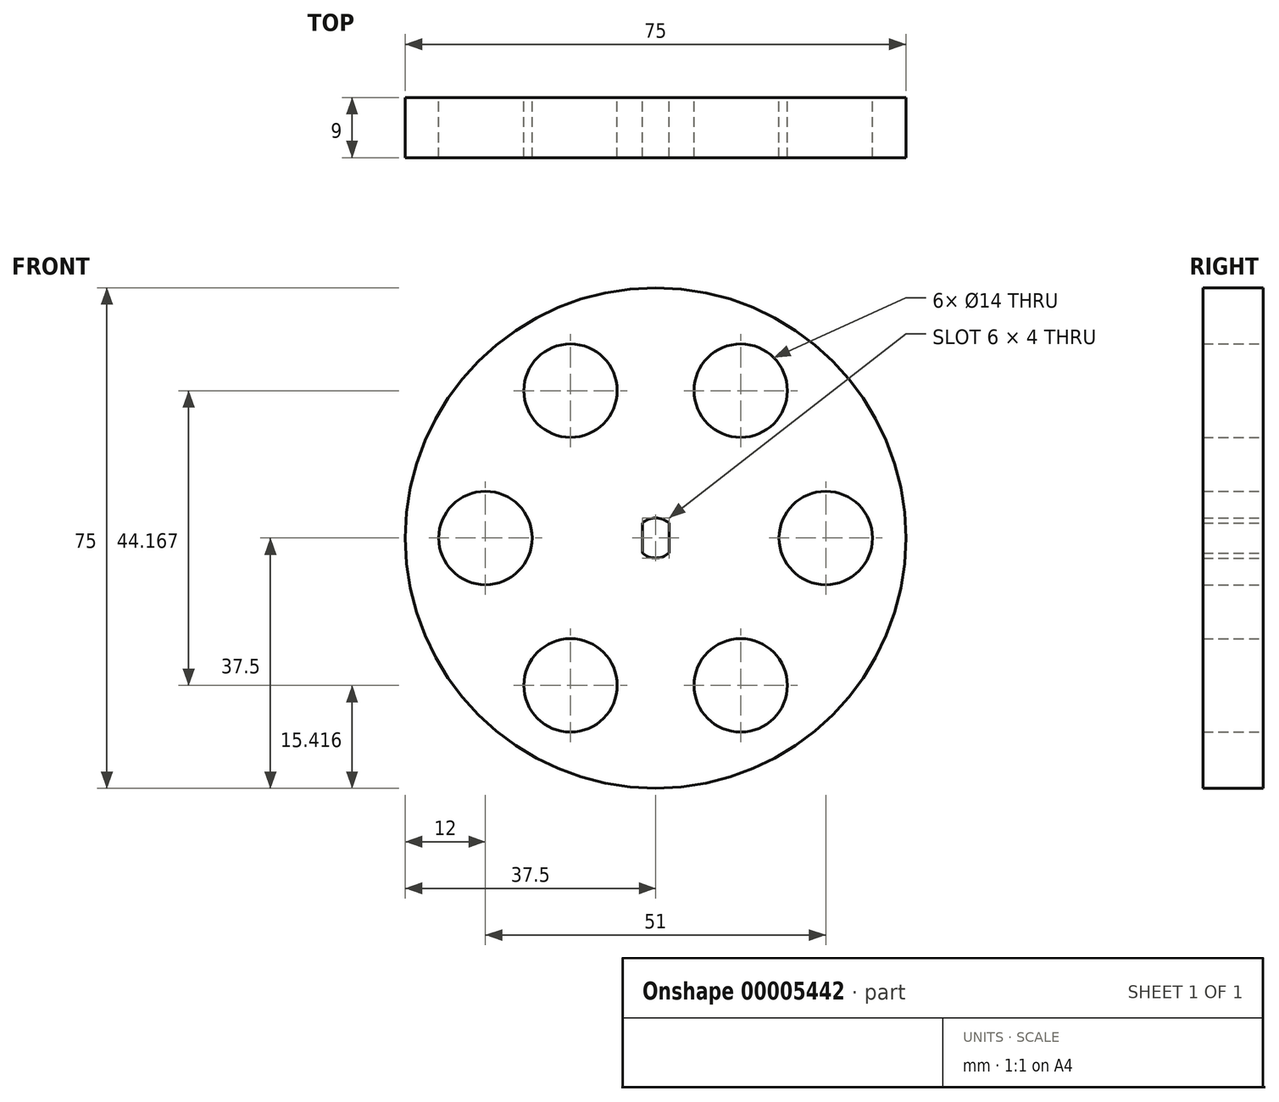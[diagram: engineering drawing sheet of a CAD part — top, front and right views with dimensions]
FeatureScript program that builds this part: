
annotation { "Feature Type Name" : "Feature", "Feature Type Description" : "" }
export const myFeature = defineFeature(function(context is Context, id is Id, definition is map)
    precondition{}
    {
        {
            var Q0;
            Q0=qCreatedBy(makeId("Front.planeOp"),FACE);
            var sketch = newSketch(context, id + "F0", { "sketchPlane" : qUnion([Q0])});
            skCircle(sketch, "E0", {"center": v(0, 0) * mm, "radius": 37.5 * mm});
            skSolve(sketch);
        }
        {
            var Q0;
            Q0=makeQuery(id+"F0.imprint","IMPRINT",FACE,{"disambiguationData":[TD([[makeQuery(id+"F0.imprint","IMPRINT",EDGE,{"derivedFrom":sQuery(id+"F0.wireOp",EDGE,"E0")}),1.0]])]});
            extrude(context, id + "F1", {"entities" : qUnion([Q0]), "depth" : 9 * mm});
        }
        {
            var Q0;
            Q0=qCreatedBy(makeId("Front.planeOp"),FACE);
            var sketch = newSketch(context, id + "F2", { "sketchPlane" : qUnion([Q0])});
            skArc(sketch, "E1", {"start": v(-2, -2.24) * mm, "mid": v(0, -3) * mm, "end": v(2, -2.24) * mm});
            skLineSegment(sketch, "E2.rect.left", {"start": v(2, 2.24) * mm, "end": v(2, -2.24) * mm});
            skLineSegment(sketch, "E2.rect.right", {"start": v(-2, 2.24) * mm, "end": v(-2, -2.24) * mm});
            skArc(sketch, "E3.trimOffspring", {"start": v(2, 2.24) * mm, "mid": v(0, 3) * mm, "end": v(-2, 2.24) * mm});
            skSolve(sketch);
        }
        {
            var Q0;
            Q0=makeQuery(id+"F2.imprint","IMPRINT",FACE,{"disambiguationData":[TD([[makeQuery(id+"F2.imprint","IMPRINT",EDGE,{"derivedFrom":sQuery(id+"F2.wireOp",EDGE,"E1")}),1.0]])]});
            extrude(context, id + "F3", {"entities" : qUnion([Q0]), "operationType" : NewBodyOperationType.REMOVE, "endBound" : BoundingType.THROUGH_ALL, "depth" : 25 * mm});
        }
        {
            var Q0;
            Q0=qCreatedBy(makeId("Front.planeOp"),FACE);
            var sketch = newSketch(context, id + "F4", { "sketchPlane" : qUnion([Q0])});
            skCircle(sketch, "E4", {"center": v(25.5, 0) * mm, "radius": 7 * mm});
            skCircle(sketch, "E5.1.0", {"center": v(12.75, 22.08) * mm, "radius": 7 * mm});
            skCircle(sketch, "E5.2.0", {"center": v(-12.75, 22.08) * mm, "radius": 7 * mm});
            skCircle(sketch, "E5.3.0", {"center": v(-25.5, 0) * mm, "radius": 7 * mm});
            skCircle(sketch, "E5.4.0", {"center": v(-12.75, -22.08) * mm, "radius": 7 * mm});
            skCircle(sketch, "E5.5.0", {"center": v(12.75, -22.08) * mm, "radius": 7 * mm});
            skPoint(sketch, "E5.center", {"position": v(0, 0) * mm});
            skSolve(sketch);
        }
        {
            var Q0;
            Q0 = qSketchRegion(id + "F4", true);
            extrude(context, id + "F5", {"entities" : qUnion([Q0]), "operationType" : NewBodyOperationType.REMOVE, "endBound" : BoundingType.THROUGH_ALL, "depth" : 25 * mm});
        }
    });
